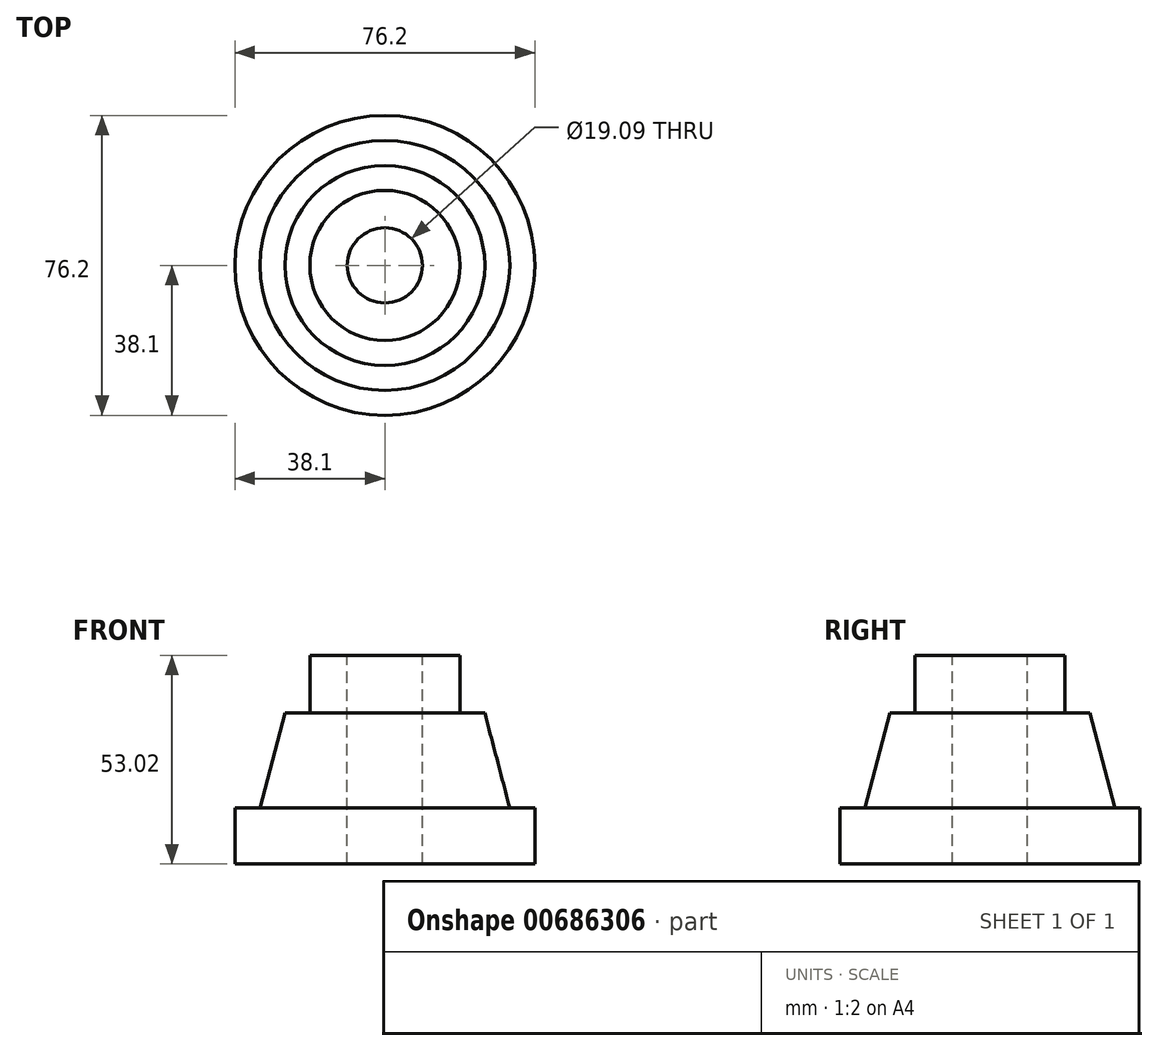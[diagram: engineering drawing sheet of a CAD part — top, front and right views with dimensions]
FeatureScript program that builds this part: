
annotation { "Feature Type Name" : "Feature", "Feature Type Description" : "" }
export const myFeature = defineFeature(function(context is Context, id is Id, definition is map)
    precondition{}
    {
        {
            var Q0;
            Q0=qCreatedBy(makeId("Front.planeOp"),FACE);
            var sketch = newSketch(context, id + "F0", { "sketchPlane" : qUnion([Q0])});
            skLineSegment(sketch, "E0", {"start": v(-25.4, 23.4) * mm, "end": v(-25.4, -29.62) * mm});
            skLineSegment(sketch, "E1", {"start": v(-25.4, -29.62) * mm, "end": v(12.7, -29.62) * mm});
            skLineSegment(sketch, "E2", {"start": v(12.7, -29.62) * mm, "end": v(12.7, -15.4) * mm});
            skLineSegment(sketch, "E3", {"start": v(12.7, -15.4) * mm, "end": v(6.35, -15.4) * mm});
            skLineSegment(sketch, "E4", {"start": v(6.35, -15.4) * mm, "end": v(0, 8.73) * mm});
            skLineSegment(sketch, "E5", {"start": v(0, 8.73) * mm, "end": v(-6.35, 8.73) * mm});
            skLineSegment(sketch, "E6", {"start": v(-6.35, 8.73) * mm, "end": v(-6.35, 23.4) * mm});
            skLineSegment(sketch, "E7", {"start": v(-6.35, 23.4) * mm, "end": v(-25.4, 23.4) * mm});
            skSolve(sketch);
        }
        {
            var Q0;
            Q0=makeQuery(id+"F0.imprint","IMPRINT",FACE,{"disambiguationData":[TD([[makeQuery(id+"F0.imprint","IMPRINT",EDGE,{"derivedFrom":sQuery(id+"F0.wireOp",EDGE,"E0")}),1.0]])]});
            var Q1;
            Q1=sQuery(id+"F0.wireOp",EDGE,"E0");
            revolve(context, id + "F1", {"entities" : qUnion([Q0]), "axis" : qUnion([Q1]), "revolveType" : RevolveType.FULL});
        }
        {
            var Q0;
            Q0=makeQuery(id+"F1.opRevolve","SWEPT_FACE",FACE,{"disambiguationData":[OSD([sQuery(id+"F0.wireOp",EDGE,"E7")])]});
            var sketch = newSketch(context, id + "F2", { "sketchPlane" : qUnion([Q0])});
            skCircle(sketch, "E8", {"center": v(-25.4, 0) * mm, "radius": 9.55 * mm});
            skSolve(sketch);
        }
        {
            var Q0;
            Q0=makeQuery(id+"F2.imprint","IMPRINT",FACE,{"disambiguationData":[TD([[makeQuery(id+"F2.imprint","IMPRINT",EDGE,{"derivedFrom":sQuery(id+"F2.wireOp",EDGE,"E8")}),1.0]])]});
            extrude(context, id + "F3", {"entities" : qUnion([Q0]), "operationType" : NewBodyOperationType.REMOVE, "endBound" : BoundingType.THROUGH_ALL, "oppositeDirection" : true, "depth" : 25.4 * mm, "offsetDistance" : 25.4 * mm});
        }
    });
